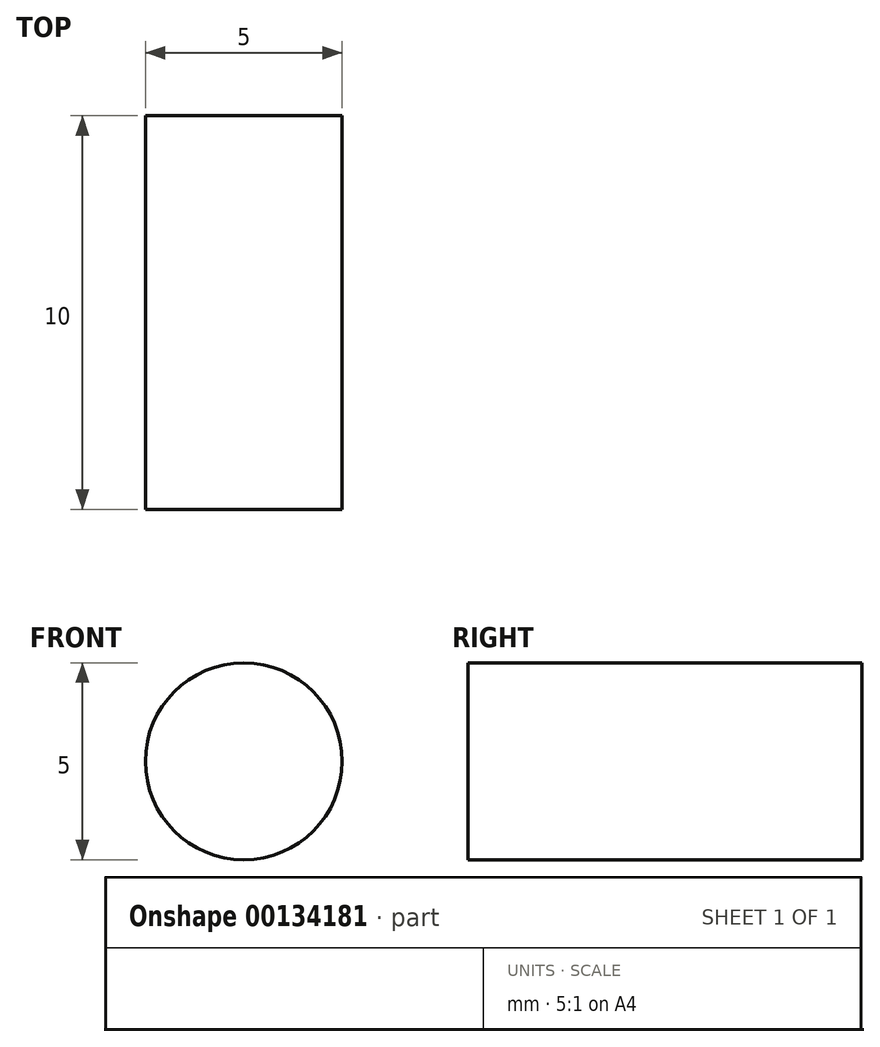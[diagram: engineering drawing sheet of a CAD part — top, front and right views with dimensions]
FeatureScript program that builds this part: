
annotation { "Feature Type Name" : "Feature", "Feature Type Description" : "" }
export const myFeature = defineFeature(function(context is Context, id is Id, definition is map)
    precondition{}
    {
        {
            var Q0;
            Q0=qCreatedBy(makeId("Front.planeOp"),FACE);
            var sketch = newSketch(context, id + "F0", { "sketchPlane" : qUnion([Q0])});
            skCircle(sketch, "E0", {"center": v(0, 0) * mm, "radius": 2.5 * mm});
            skSolve(sketch);
        }
        {
            var Q0;
            Q0=makeQuery(id+"F0.imprint","IMPRINT",FACE,{"disambiguationData":[TD([[makeQuery(id+"F0.imprint","IMPRINT",EDGE,{"derivedFrom":sQuery(id+"F0.wireOp",EDGE,"E0")}),1.0]])]});
            extrude(context, id + "F1", {"entities" : qUnion([Q0]), "depth" : 10 * mm});
        }
    });
